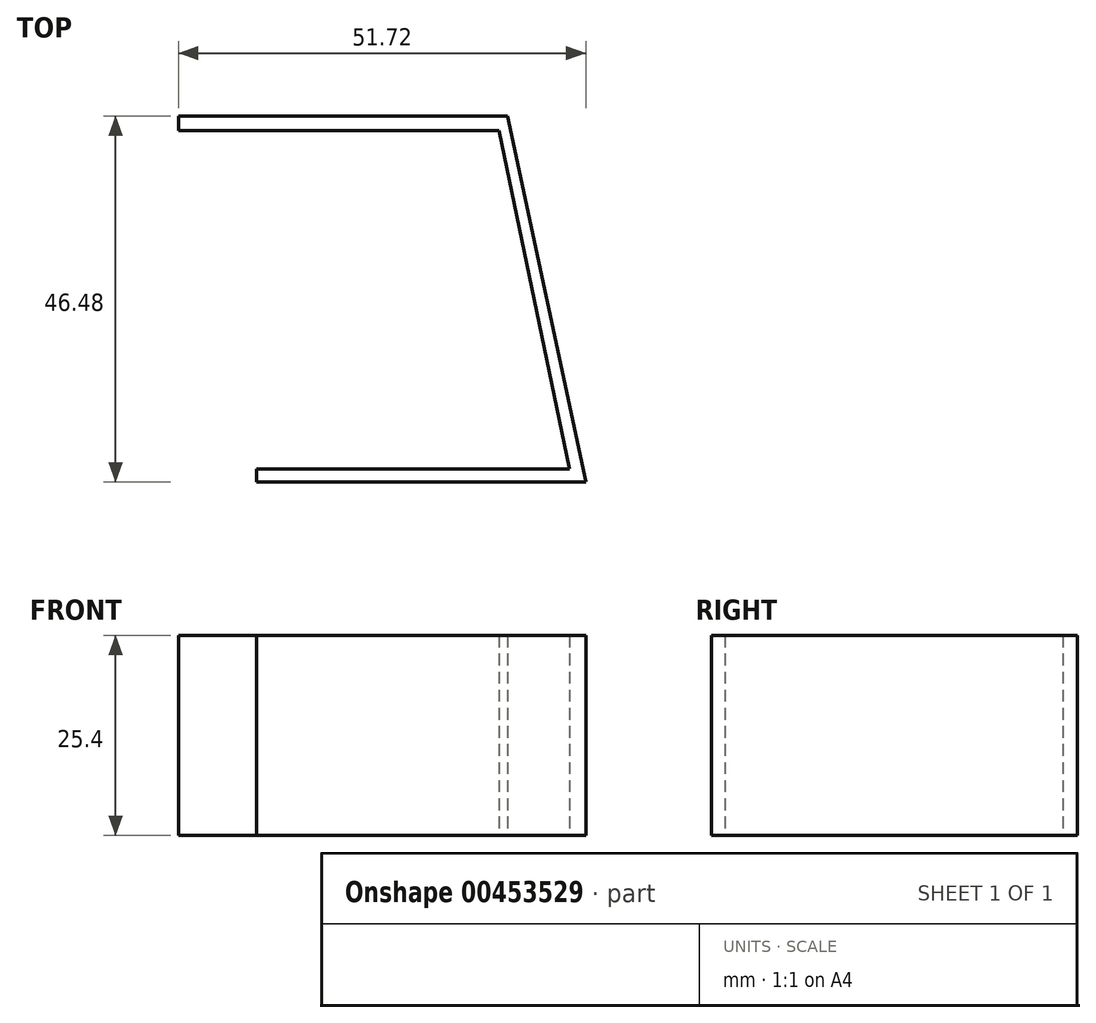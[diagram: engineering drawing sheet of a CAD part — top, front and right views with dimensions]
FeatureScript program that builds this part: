
annotation { "Feature Type Name" : "Feature", "Feature Type Description" : "" }
export const myFeature = defineFeature(function(context is Context, id is Id, definition is map)
    precondition{}
    {
        {
            var Q0;
            Q0=qCreatedBy(makeId("Top.planeOp"),FACE);
            var sketch = newSketch(context, id + "F0", { "sketchPlane" : qUnion([Q0])});
            skLineSegment(sketch, "E0", {"start": v(0, 0) * mm, "end": v(-41.8, 0) * mm});
            skLineSegment(sketch, "E1", {"start": v(-41.8, 0) * mm, "end": v(-41.8, 1.68) * mm});
            skLineSegment(sketch, "E2", {"start": v(-41.8, 1.68) * mm, "end": v(-2.06, 1.68) * mm});
            skLineSegment(sketch, "E3", {"start": v(-2.06, 1.68) * mm, "end": v(-11.03, 44.63) * mm});
            skLineSegment(sketch, "E4", {"start": v(-11.03, 44.63) * mm, "end": v(-51.72, 44.63) * mm});
            skLineSegment(sketch, "E5", {"start": v(-51.72, 44.63) * mm, "end": v(-51.72, 46.48) * mm});
            skLineSegment(sketch, "E6", {"start": v(-51.72, 46.48) * mm, "end": v(-9.95, 46.48) * mm});
            skLineSegment(sketch, "E7", {"start": v(-9.95, 46.48) * mm, "end": v(0, 0) * mm});
            skSolve(sketch);
        }
        {
            var Q0;
            Q0=makeQuery(id+"F0.imprint","IMPRINT",FACE,{"disambiguationData":[TD([[makeQuery(id+"F0.imprint","IMPRINT",EDGE,{"derivedFrom":sQuery(id+"F0.wireOp",EDGE,"E0")}),-1.0]])]});
            extrude(context, id + "F1", {"entities" : qUnion([Q0]), "depth" : 25.4 * mm});
        }
    });
